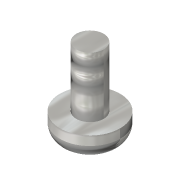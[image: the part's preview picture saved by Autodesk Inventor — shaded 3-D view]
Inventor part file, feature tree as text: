
AUTODESK INVENTOR PART (.ipt)
format: ipt  version: 2016 SP1 (Build 200210100, 210)  size: 140,288 bytes
history: native  units: mm
features: extrude x3, sketch x3, fillet x1
ambient origin geometry x8: Origin, YZ Plane, XZ Plane, XY Plane, X Axis, Y Axis, Z Axis, Center Point
bodies: Volumenkörper1 (feature_tree)
feature tree (7):
  extrude  "Extrusion1"  Depth=1.3mm TaperAngle=0.0deg
  extrude  "Extrusion2"  Depth=3.3mm TaperAngle=0.0deg
  extrude  "Extrusion3"  Depth=0.55mm
  fillet  "Rundung1"  Radius=2.4mm
  sketch  "Skizze1"  dims[d0=3.3mm d1=1.3mm d2=0.0mm]
  sketch  "Skizze2"  dims[d3=1.5mm d4=3.3mm d5=0.0mm]
  sketch  "Skizze3"  dims[d6=0.55mm d7=0.55mm d8=2.4mm d9=2.4mm d10=1.0mm d11=0.0mm d12=0.8mm]
